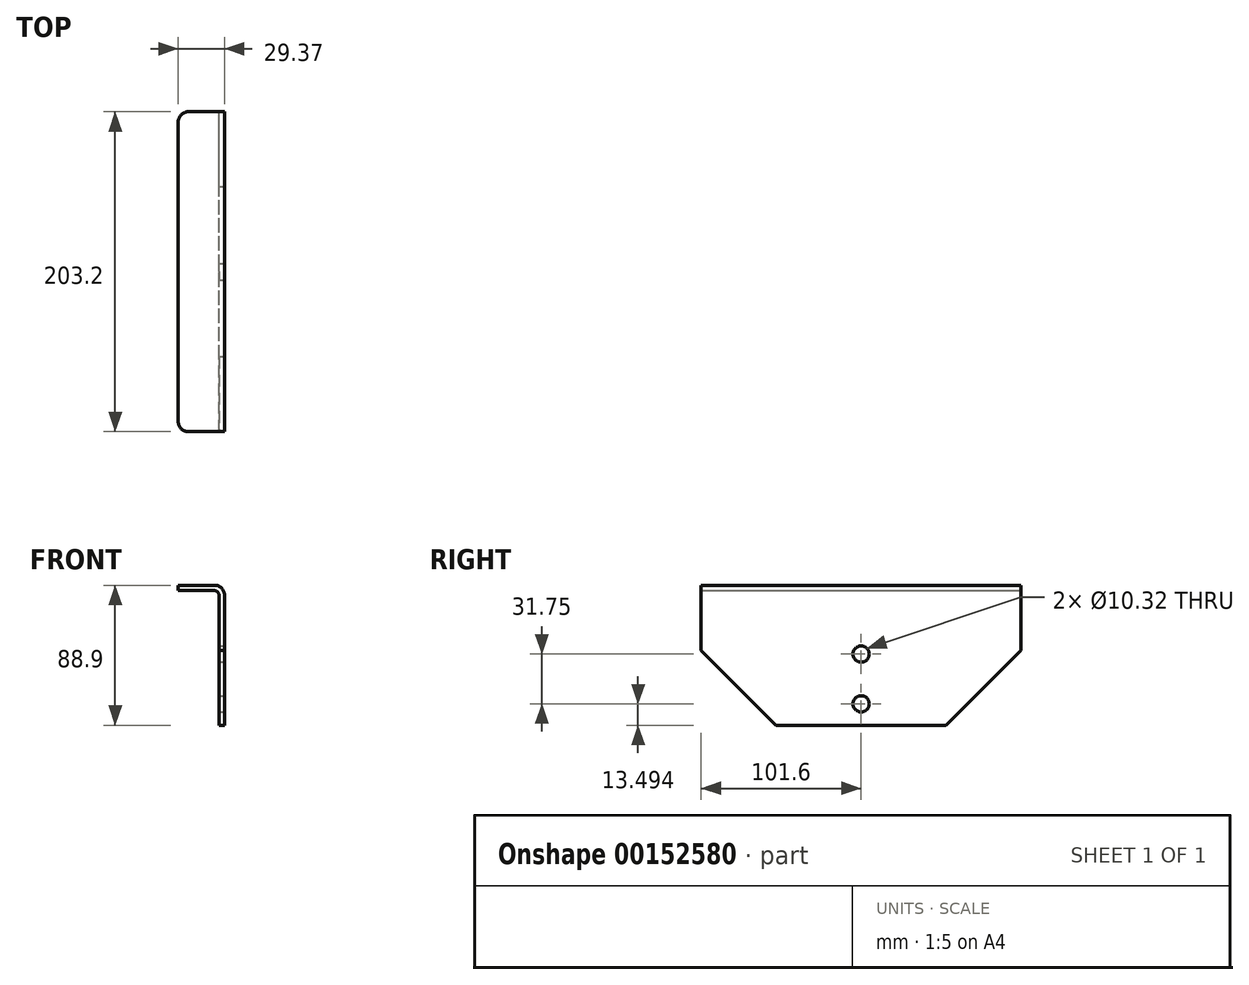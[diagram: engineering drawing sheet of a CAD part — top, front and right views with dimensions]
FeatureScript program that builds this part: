
annotation { "Feature Type Name" : "Feature", "Feature Type Description" : "" }
export const myFeature = defineFeature(function(context is Context, id is Id, definition is map)
    precondition{}
    {
        {
            var Q0;
            Q0=qCreatedBy(makeId("Front.planeOp"),FACE);
            var sketch = newSketch(context, id + "F0", { "sketchPlane" : qUnion([Q0])});
            skLineSegment(sketch, "E0", {"start": v(-25.94, 88.9) * mm, "end": v(-2.92, 88.9) * mm});
            skLineSegment(sketch, "E1", {"start": v(3.43, 82.55) * mm, "end": v(3.43, 0) * mm});
            skLineSegment(sketch, "E2", {"start": v(3.43, 0) * mm, "end": v(0, 0) * mm});
            skLineSegment(sketch, "E3", {"start": v(0, 0) * mm, "end": v(0, 82.3) * mm});
            skLineSegment(sketch, "E4", {"start": v(-3.18, 85.47) * mm, "end": v(-25.94, 85.47) * mm});
            skLineSegment(sketch, "E5", {"start": v(-25.94, 85.47) * mm, "end": v(-25.94, 88.9) * mm});
            skPoint(sketch, "E6.visualSharp", {"position": v(0, 85.47) * mm});
            skArc(sketch, "E6.filletArc", {"start": v(0, 82.3) * mm, "mid": v(-0.93, 84.54) * mm, "end": v(-3.18, 85.47) * mm});
            skPoint(sketch, "E7.visualSharp", {"position": v(3.43, 88.9) * mm});
            skArc(sketch, "E7.filletArc", {"start": v(3.43, 82.55) * mm, "mid": v(1.57, 87.04) * mm, "end": v(-2.92, 88.9) * mm});
            skSolve(sketch);
        }
        {
            var Q0;
            Q0=makeQuery(id+"F0.imprint","IMPRINT",FACE,{"disambiguationData":[TD([[makeQuery(id+"F0.imprint","IMPRINT",EDGE,{"derivedFrom":sQuery(id+"F0.wireOp",EDGE,"E0")}),-1.0]])]});
            extrude(context, id + "F1", {"entities" : qUnion([Q0]), "endBound" : BoundingType.SYMMETRIC, "depth" : 203.2 * mm});
        }
        {
            var Q0;
            Q0=makeQuery(id+"F1.opExtrude","SWEPT_FACE",FACE,{"disambiguationData":[OSD([sQuery(id+"F0.wireOp",EDGE,"E1")])]});
            var sketch = newSketch(context, id + "F2", { "sketchPlane" : qUnion([Q0])});
            skLineSegment(sketch, "E8", {"start": v(-101.6, 47.62) * mm, "end": v(101.6, 47.63) * mm});
            skLineSegment(sketch, "E9", {"start": v(-101.6, 47.62) * mm, "end": v(-53.97, 0) * mm});
            skLineSegment(sketch, "E10", {"start": v(101.6, 47.63) * mm, "end": v(53.97, 0) * mm});
            skLineSegment(sketch, "E11", {"start": v(-101.6, 47.62) * mm, "end": v(-101.6, 0) * mm});
            skLineSegment(sketch, "E12", {"start": v(-101.6, 0) * mm, "end": v(-53.97, 0) * mm});
            skLineSegment(sketch, "E13", {"start": v(53.97, 0) * mm, "end": v(101.6, 0) * mm});
            skLineSegment(sketch, "E14", {"start": v(101.6, 0) * mm, "end": v(101.6, 47.63) * mm});
            skSolve(sketch);
        }
        {
            var Q0;
            Q0=makeQuery(id+"F2.imprint","IMPRINT",FACE,{"disambiguationData":[TD([[makeQuery(id+"F2.imprint","IMPRINT",EDGE,{"derivedFrom":sQuery(id+"F2.wireOp",EDGE,"E9")}),-1.0]])]});
            var Q1;
            Q1=makeQuery(id+"F2.imprint","IMPRINT",FACE,{"disambiguationData":[TD([[makeQuery(id+"F2.imprint","IMPRINT",EDGE,{"derivedFrom":sQuery(id+"F2.wireOp",EDGE,"E10")}),1.0]])]});
            extrude(context, id + "F3", {"entities" : qUnion([Q0, Q1]), "operationType" : NewBodyOperationType.REMOVE, "oppositeDirection" : true, "depth" : 25.4 * mm, "hasSecondDirection" : true, "secondDirectionOppositeDirection" : false, "secondDirectionDepth" : 25.4 * mm});
        }
        {
            var Q0;
            Q0=makeQuery(id+"F3.boolean.opBoolean","COPY",EDGE,{"derivedFrom":makeQuery(id+"F3.opExtrude","SWEPT_EDGE",EDGE,{"disambiguationData":[OSD([sQuery(id+"F0.wireOp",EDGE,"E1"),sQuery(id+"F2.wireOp",EDGE,"E8"),sQuery(id+"F2.wireOp",EDGE,"E9"),sQuery(id+"F2.wireOp",EDGE,"E11")])]})});
            var Q1;
            Q1=makeQuery(id+"F1.opExtrude","CAP_EDGE",EDGE,{"disambiguationData":[OSD([sQuery(id+"F0.wireOp",EDGE,"E5")])],"isStart":false});
            var Q2;
            Q2=makeQuery(id+"F3.boolean.opBoolean","COPY",EDGE,{"derivedFrom":makeQuery(id+"F3.opExtrude","SWEPT_EDGE",EDGE,{"disambiguationData":[OSD([sQuery(id+"F0.wireOp",EDGE,"E1"),sQuery(id+"F0.wireOp",EDGE,"E2"),sQuery(id+"F2.wireOp",EDGE,"E9"),sQuery(id+"F2.wireOp",EDGE,"E12")])]})});
            var Q3;
            Q3=makeQuery(id+"F3.boolean.opBoolean","COPY",EDGE,{"derivedFrom":makeQuery(id+"F3.opExtrude","SWEPT_EDGE",EDGE,{"disambiguationData":[OSD([sQuery(id+"F0.wireOp",EDGE,"E1"),sQuery(id+"F0.wireOp",EDGE,"E2"),sQuery(id+"F2.wireOp",EDGE,"E10"),sQuery(id+"F2.wireOp",EDGE,"E13")])]})});
            var Q4;
            Q4=makeQuery(id+"F3.boolean.opBoolean","COPY",EDGE,{"derivedFrom":makeQuery(id+"F3.opExtrude","SWEPT_EDGE",EDGE,{"disambiguationData":[OSD([sQuery(id+"F0.wireOp",EDGE,"E1"),sQuery(id+"F2.wireOp",EDGE,"E8"),sQuery(id+"F2.wireOp",EDGE,"E10"),sQuery(id+"F2.wireOp",EDGE,"E14")])]})});
            var Q5;
            Q5=makeQuery(id+"F1.opExtrude","CAP_EDGE",EDGE,{"disambiguationData":[OSD([sQuery(id+"F0.wireOp",EDGE,"E5")])],"isStart":true});
            fillet(context, id + "F4", {"entities" : qUnion([Q0, Q1, Q2, Q3, Q4, Q5]), "radius" : 6.35 * mm, "tangentPropagation" : true, "allowEdgeOverflow" : false});
        }
        {
            var Q0;
            Q0=makeQuery(id+"F1.opExtrude","SWEPT_FACE",FACE,{"disambiguationData":[OSD([sQuery(id+"F0.wireOp",EDGE,"E1")])]});
            var sketch = newSketch(context, id + "F5", { "sketchPlane" : qUnion([Q0])});
            skCircle(sketch, "E15", {"center": v(0, 45.24) * mm, "radius": 5.16 * mm});
            skCircle(sketch, "E16", {"center": v(0, 13.5) * mm, "radius": 5.16 * mm});
            skSolve(sketch);
        }
        {
            var Q0;
            Q0=makeQuery(id+"F5.imprint","IMPRINT",FACE,{"disambiguationData":[TD([[makeQuery(id+"F5.imprint","IMPRINT",EDGE,{"derivedFrom":sQuery(id+"F5.wireOp",EDGE,"E15")}),1.0]])]});
            var Q1;
            Q1=makeQuery(id+"F5.imprint","IMPRINT",FACE,{"disambiguationData":[TD([[makeQuery(id+"F5.imprint","IMPRINT",EDGE,{"derivedFrom":sQuery(id+"F5.wireOp",EDGE,"E16")}),1.0]])]});
            extrude(context, id + "F6", {"entities" : qUnion([Q0, Q1]), "operationType" : NewBodyOperationType.REMOVE, "oppositeDirection" : true, "depth" : 25.4 * mm, "hasSecondDirection" : true, "secondDirectionOppositeDirection" : false, "secondDirectionDepth" : 25.4 * mm});
        }
    });
